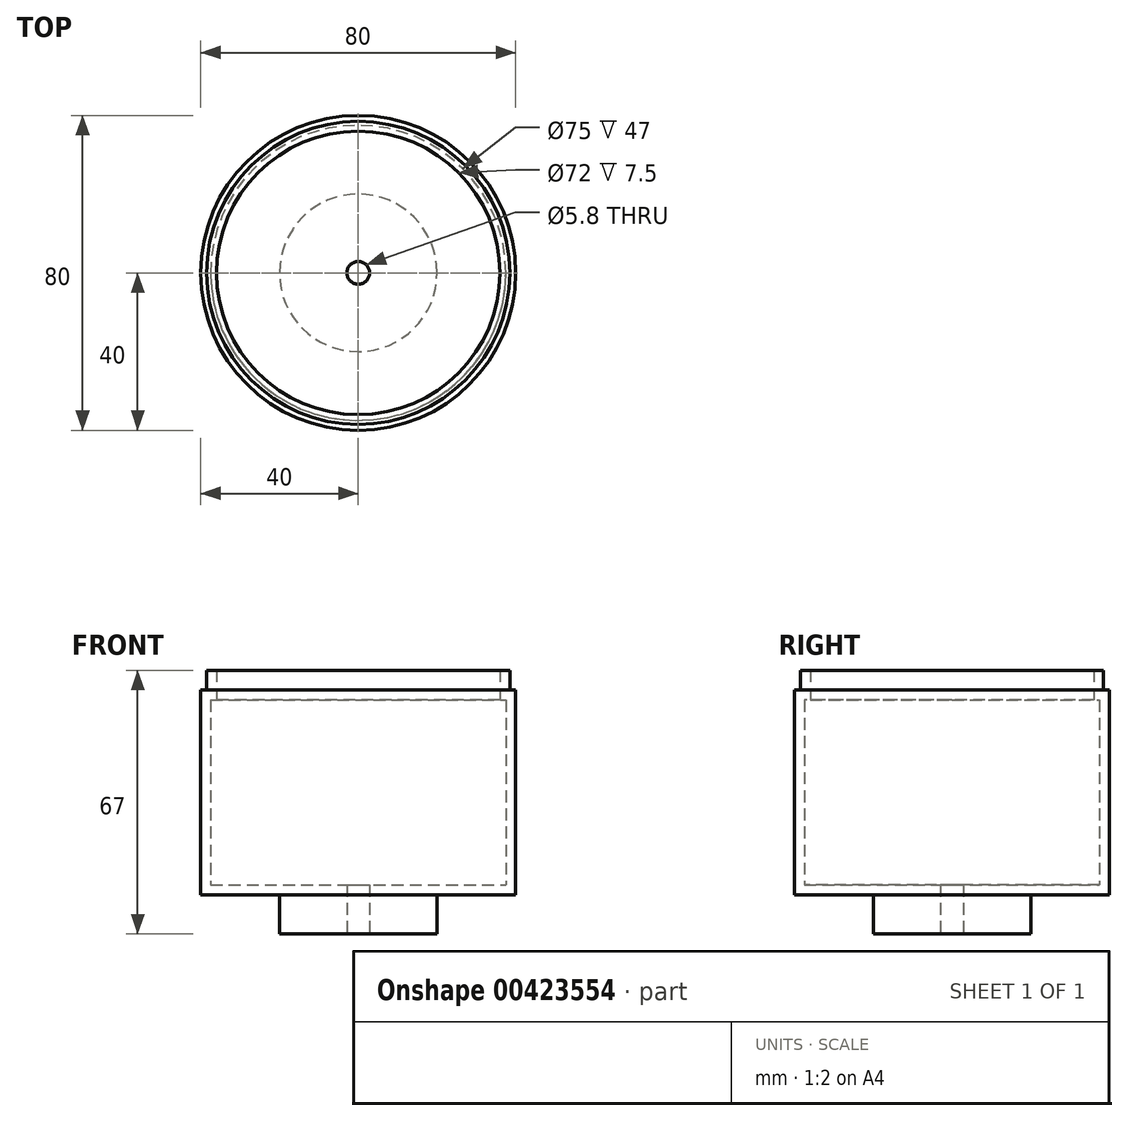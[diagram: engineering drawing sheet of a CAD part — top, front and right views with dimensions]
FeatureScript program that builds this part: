
annotation { "Feature Type Name" : "Feature", "Feature Type Description" : "" }
export const myFeature = defineFeature(function(context is Context, id is Id, definition is map)
    precondition{}
    {
        {
            var Q0;
            Q0=qCreatedBy(makeId("Top.planeOp"),FACE);
            var sketch = newSketch(context, id + "F0", { "sketchPlane" : qUnion([Q0])});
            skCircle(sketch, "E0", {"center": v(0, 0) * mm, "radius": 40 * mm});
            skSolve(sketch);
        }
        {
            var Q0;
            Q0=makeQuery(id+"F0.imprint","IMPRINT",FACE,{"disambiguationData":[TD([[makeQuery(id+"F0.imprint","IMPRINT",EDGE,{"derivedFrom":sQuery(id+"F0.wireOp",EDGE,"E0")}),1.0]])]});
            extrude(context, id + "F1", {"entities" : qUnion([Q0]), "depth" : 2 * mm});
        }
        {
            var Q0;
            Q0=makeQuery(id+"F1.opExtrude","CAP_FACE",FACE,{"disambiguationData":[OSD([sQuery(id+"F0.wireOp",EDGE,"E0")])],"isStart":false});
            var sketch = newSketch(context, id + "F2", { "sketchPlane" : qUnion([Q0])});
            skCircle(sketch, "E1", {"center": v(0, 0) * mm, "radius": 38.5 * mm});
            skSolve(sketch);
        }
        {
            var Q0;
            Q0=makeQuery(id+"F2.imprint","IMPRINT",FACE,{"disambiguationData":[TD([[makeQuery(id+"F2.imprint","IMPRINT",EDGE,{"derivedFrom":sQuery(id+"F2.wireOp",EDGE,"E1")}),1.0]])]});
            extrude(context, id + "F3", {"entities" : qUnion([Q0]), "operationType" : NewBodyOperationType.ADD, "depth" : 5 * mm});
        }
        {
            var Q0;
            Q0=makeQuery(id+"F1.opExtrude","CAP_FACE",FACE,{"disambiguationData":[OSD([sQuery(id+"F0.wireOp",EDGE,"E0")])],"isStart":true});
            var sketch = newSketch(context, id + "F4", { "sketchPlane" : qUnion([Q0])});
            skSolve(sketch);
        }
        {
            var Q0;
            Q0=makeQuery(id+"F4.imprint","IMPRINT",FACE,{"disambiguationData":[TD([[makeQuery(id+"F4.imprint","IMPRINT",EDGE,{"derivedFrom":makeQuery(id+"F1.opExtrude","CAP_EDGE",EDGE,{"disambiguationData":[OSD([sQuery(id+"F0.wireOp",EDGE,"E0")])],"isStart":true})}),-1.0]])]});
            extrude(context, id + "F5", {"entities" : qUnion([Q0]), "operationType" : NewBodyOperationType.ADD, "depth" : 50 * mm});
        }
        {
            var Q0;
            Q0=makeQuery(id+"F5.opExtrude","CAP_FACE",FACE,{"disambiguationData":[OSD([sQuery(id+"F0.wireOp",EDGE,"E0")])],"isStart":false});
            var sketch = newSketch(context, id + "F6", { "sketchPlane" : qUnion([Q0])});
            skCircle(sketch, "E2", {"center": v(0, 0) * mm, "radius": 20 * mm});
            skSolve(sketch);
        }
        {
            var Q0;
            Q0=makeQuery(id+"F3.opExtrude","CAP_FACE",FACE,{"disambiguationData":[OSD([sQuery(id+"F2.wireOp",EDGE,"E1")])],"isStart":false});
            shell(context, id + "F7", {"entities" : qUnion([Q0]), "thickness" : 2.5 * mm});
        }
        {
            var Q0;
            Q0=makeQuery(id+"F6.imprint","IMPRINT",FACE,{"disambiguationData":[TD([[makeQuery(id+"F6.imprint","IMPRINT",EDGE,{"derivedFrom":sQuery(id+"F6.wireOp",EDGE,"E2")}),1.0]])]});
            extrude(context, id + "F8", {"entities" : qUnion([Q0]), "operationType" : NewBodyOperationType.ADD, "depth" : 10 * mm});
        }
        {
            var Q0;
            Q0=makeQuery(id+"F8.opExtrude","CAP_FACE",FACE,{"disambiguationData":[OSD([sQuery(id+"F6.wireOp",EDGE,"E2")])],"isStart":false});
            var sketch = newSketch(context, id + "F9", { "sketchPlane" : qUnion([Q0])});
            skCircle(sketch, "E3", {"center": v(0, 0) * mm, "radius": 2.9 * mm});
            skSolve(sketch);
        }
        {
            var Q0;
            Q0=makeQuery(id+"F9.imprint","IMPRINT",FACE,{"disambiguationData":[TD([[makeQuery(id+"F9.imprint","IMPRINT",EDGE,{"derivedFrom":sQuery(id+"F9.wireOp",EDGE,"E3")}),1.0]])]});
            extrude(context, id + "F10", {"entities" : qUnion([Q0]), "operationType" : NewBodyOperationType.REMOVE, "endBound" : BoundingType.THROUGH_ALL, "oppositeDirection" : true, "depth" : 25 * mm});
        }
    });
